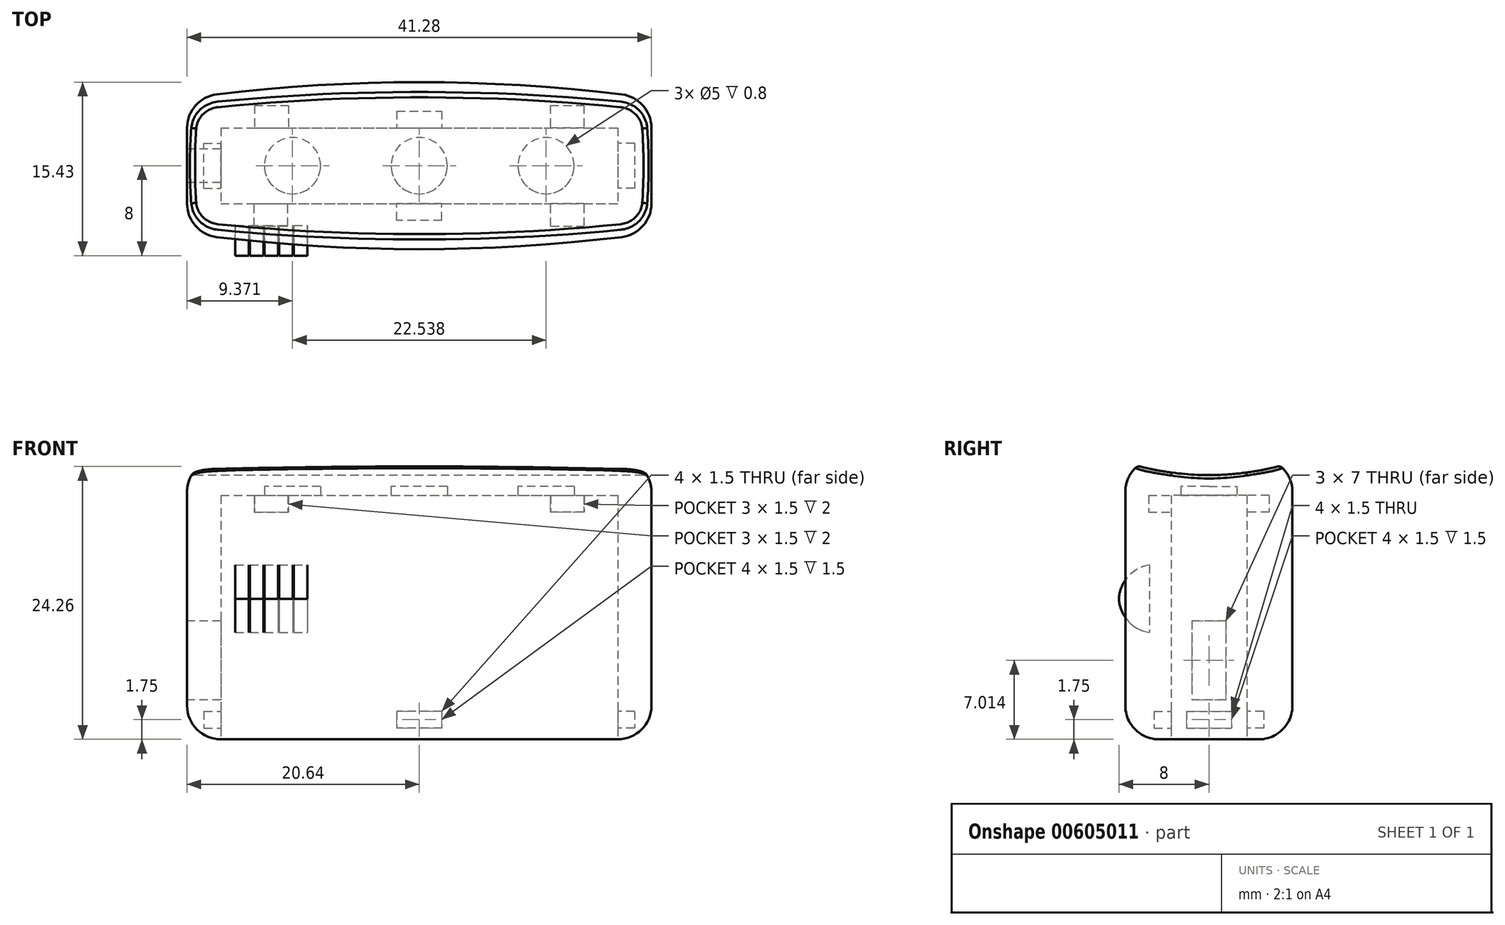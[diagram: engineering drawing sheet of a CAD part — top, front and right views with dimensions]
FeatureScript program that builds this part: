
annotation { "Feature Type Name" : "Feature", "Feature Type Description" : "" }
export const myFeature = defineFeature(function(context is Context, id is Id, definition is map)
    precondition{}
    {
        {
            var Q0;
            Q0=qCreatedBy(makeId("Top.planeOp"),FACE);
            var sketch = newSketch(context, id + "F0", { "sketchPlane" : qUnion([Q0])});
            skLineSegment(sketch, "E0", {"start": v(-20.64, 6) * mm, "end": v(-20.64, -6) * mm});
            skLineSegment(sketch, "E1", {"start": v(20.64, 6) * mm, "end": v(20.64, -6) * mm});
            skArc(sketch, "E2", {"start": v(20.64, 6) * mm, "mid": v(0, 7.43) * mm, "end": v(-20.64, 6) * mm});
            skArc(sketch, "E3.MirrorCS", {"start": v(20.64, -6) * mm, "mid": v(0, -7.43) * mm, "end": v(-20.64, -6) * mm});
            skSolve(sketch);
        }
        {
            var Q0;
            Q0=qSketchRegion(id+"F0",true);
            extrude(context, id + "F1", {"entities" : qUnion([Q0]), "depth" : 25 * mm, "offsetDistance" : 25 * mm});
        }
        {
            var Q0;
            Q0=makeQuery(id+"F1.opExtrude","SWEPT_EDGE",EDGE,{"disambiguationData":[OSD([sQuery(id+"F0.wireOp",EDGE,"E0"),sQuery(id+"F0.wireOp",EDGE,"E2")])]});
            var Q1;
            Q1=makeQuery(id+"F1.opExtrude","SWEPT_EDGE",EDGE,{"disambiguationData":[OSD([sQuery(id+"F0.wireOp",EDGE,"E0"),sQuery(id+"F0.wireOp",EDGE,"E3.MirrorCS")])]});
            var Q2;
            Q2=makeQuery(id+"F1.opExtrude","SWEPT_EDGE",EDGE,{"disambiguationData":[OSD([sQuery(id+"F0.wireOp",EDGE,"E1"),sQuery(id+"F0.wireOp",EDGE,"E2")])]});
            var Q3;
            Q3=makeQuery(id+"F1.opExtrude","SWEPT_EDGE",EDGE,{"disambiguationData":[OSD([sQuery(id+"F0.wireOp",EDGE,"E1"),sQuery(id+"F0.wireOp",EDGE,"E3.MirrorCS")])]});
            var Q4;
            Q4=makeQuery(id+"F1.opExtrude","CAP_EDGE",EDGE,{"disambiguationData":[OSD([sQuery(id+"F0.wireOp",EDGE,"E2")])],"isStart":true});
            var Q5;
            Q5=makeQuery(id+"F1.opExtrude","CAP_EDGE",EDGE,{"disambiguationData":[OSD([sQuery(id+"F0.wireOp",EDGE,"E3.MirrorCS")])],"isStart":true});
            var Q6;
            Q6=makeQuery(id+"F1.opExtrude","CAP_EDGE",EDGE,{"disambiguationData":[OSD([sQuery(id+"F0.wireOp",EDGE,"E0")])],"isStart":true});
            var Q7;
            Q7=makeQuery(id+"F1.opExtrude","CAP_EDGE",EDGE,{"disambiguationData":[OSD([sQuery(id+"F0.wireOp",EDGE,"E1")])],"isStart":true});
            var Q8;
            Q8=makeQuery(id+"F1.opExtrude","CAP_FACE",FACE,{"disambiguationData":[OSD([sQuery(id+"F0.wireOp",EDGE,"E0"),sQuery(id+"F0.wireOp",EDGE,"E1"),sQuery(id+"F0.wireOp",EDGE,"E2"),sQuery(id+"F0.wireOp",EDGE,"E3.MirrorCS")])],"isStart":false});
            fillet(context, id + "F2", {"entities" : qUnion([Q0, Q1, Q2, Q3, Q4, Q5, Q6, Q7, Q8]), "radius" : 3 * mm, "tangentPropagation" : true, "allowEdgeOverflow" : false});
        }
        {
            var Q0;
            Q0=makeQuery(id+"F1.opExtrude","SWEPT_FACE",FACE,{"disambiguationData":[OSD([sQuery(id+"F0.wireOp",EDGE,"E1")])]});
            var sketch = newSketch(context, id + "F3", { "sketchPlane" : qUnion([Q0])});
            skCircle(sketch, "E4", {"center": v(0, 48.5) * mm, "radius": 25 * mm});
            skSolve(sketch);
        }
        {
            var Q0;
            Q0=qSketchRegion(id+"F3",true);
            extrude(context, id + "F4", {"entities" : qUnion([Q0]), "operationType" : NewBodyOperationType.REMOVE, "oppositeDirection" : true, "depth" : 48.9 * mm, "offsetDistance" : 25 * mm});
        }
        {
            var Q0;
            Q0=makeQuery(id+"F1.opExtrude","CAP_FACE",FACE,{"disambiguationData":[OSD([sQuery(id+"F0.wireOp",EDGE,"E0"),sQuery(id+"F0.wireOp",EDGE,"E1"),sQuery(id+"F0.wireOp",EDGE,"E2"),sQuery(id+"F0.wireOp",EDGE,"E3.MirrorCS")])],"isStart":true});
            var sketch = newSketch(context, id + "F5", { "sketchPlane" : qUnion([Q0])});
            skLineSegment(sketch, "E5.bottom", {"start": v(-17.64, 3.36) * mm, "end": v(17.64, 3.36) * mm});
            skLineSegment(sketch, "E5.top", {"start": v(-17.64, -3.36) * mm, "end": v(17.64, -3.36) * mm});
            skLineSegment(sketch, "E5.left", {"start": v(-17.64, 3.36) * mm, "end": v(-17.64, -3.36) * mm});
            skLineSegment(sketch, "E5.right", {"start": v(17.64, 3.36) * mm, "end": v(17.64, -3.36) * mm});
            skSolve(sketch);
        }
        {
            var Q0;
            Q0=qSketchRegion(id+"F5",true);
            extrude(context, id + "F6", {"entities" : qUnion([Q0]), "operationType" : NewBodyOperationType.REMOVE, "oppositeDirection" : true, "depth" : 21.7 * mm, "offsetDistance" : 25 * mm});
        }
        {
            var Q0;
            Q0=makeQuery(id+"F1.opExtrude","SWEPT_FACE",FACE,{"disambiguationData":[OSD([sQuery(id+"F0.wireOp",EDGE,"E0")])]});
            var sketch = newSketch(context, id + "F7", { "sketchPlane" : qUnion([Q0])});
            skLineSegment(sketch, "E6.bottom", {"start": v(-1.5, 10.51) * mm, "end": v(1.5, 10.51) * mm});
            skLineSegment(sketch, "E6.top", {"start": v(-1.5, 3.51) * mm, "end": v(1.5, 3.51) * mm});
            skLineSegment(sketch, "E6.left", {"start": v(-1.5, 10.51) * mm, "end": v(-1.5, 3.51) * mm});
            skLineSegment(sketch, "E6.right", {"start": v(1.5, 10.51) * mm, "end": v(1.5, 3.51) * mm});
            skSolve(sketch);
        }
        {
            var Q0;
            Q0=qSketchRegion(id+"F7",true);
            extrude(context, id + "F8", {"entities" : qUnion([Q0]), "operationType" : NewBodyOperationType.REMOVE, "oppositeDirection" : true, "depth" : 25 * mm, "offsetDistance" : 25 * mm});
        }
        {
            var Q0;
            Q0=makeQuery(id+"F4.boolean.opBoolean","COPY",FACE,{"derivedFrom":makeQuery(id+"F4.opExtrude","SWEPT_FACE",FACE,{"disambiguationData":[OSD([sQuery(id+"F3.wireOp",EDGE,"E4")])]})});
            fillet(context, id + "F9", {"entities" : qUnion([Q0]), "radius" : 0.5 * mm, "tangentPropagation" : true, "allowEdgeOverflow" : false});
        }
        {
            var Q0;
            Q0=qCreatedBy(makeId("Front.planeOp"),FACE);
            var sketch = newSketch(context, id + "F10", { "sketchPlane" : qUnion([Q0])});
            skLineSegment(sketch, "E7.bottom", {"start": v(-15.04, 15.5) * mm, "end": v(-13.84, 15.5) * mm});
            skLineSegment(sketch, "E7.top", {"start": v(-15.04, 9.5) * mm, "end": v(-13.84, 9.5) * mm});
            skLineSegment(sketch, "E7.left", {"start": v(-15.04, 15.5) * mm, "end": v(-15.04, 9.5) * mm});
            skLineSegment(sketch, "E7.right", {"start": v(-13.84, 15.5) * mm, "end": v(-13.84, 9.5) * mm});
            skLineSegment(sketch, "E8.bottom", {"start": v(-13.74, 15.5) * mm, "end": v(-12.54, 15.5) * mm});
            skLineSegment(sketch, "E8.top", {"start": v(-13.74, 9.5) * mm, "end": v(-12.54, 9.5) * mm});
            skLineSegment(sketch, "E8.left", {"start": v(-13.74, 15.5) * mm, "end": v(-13.74, 9.5) * mm});
            skLineSegment(sketch, "E8.right", {"start": v(-12.54, 15.5) * mm, "end": v(-12.54, 9.5) * mm});
            skLineSegment(sketch, "E9.bottom", {"start": v(-12.44, 15.5) * mm, "end": v(-11.24, 15.5) * mm});
            skLineSegment(sketch, "E9.top", {"start": v(-12.44, 9.5) * mm, "end": v(-11.24, 9.5) * mm});
            skLineSegment(sketch, "E9.left", {"start": v(-12.44, 15.5) * mm, "end": v(-12.44, 9.5) * mm});
            skLineSegment(sketch, "E9.right", {"start": v(-11.24, 15.5) * mm, "end": v(-11.24, 9.5) * mm});
            skLineSegment(sketch, "E10.bottom", {"start": v(-11.14, 15.5) * mm, "end": v(-9.94, 15.5) * mm});
            skLineSegment(sketch, "E10.top", {"start": v(-11.14, 9.5) * mm, "end": v(-9.94, 9.5) * mm});
            skLineSegment(sketch, "E10.left", {"start": v(-11.14, 15.5) * mm, "end": v(-11.14, 9.5) * mm});
            skLineSegment(sketch, "E10.right", {"start": v(-9.94, 15.5) * mm, "end": v(-9.94, 9.5) * mm});
            skLineSegment(sketch, "E11.bottom", {"start": v(-16.34, 15.5) * mm, "end": v(-15.14, 15.5) * mm});
            skLineSegment(sketch, "E11.top", {"start": v(-16.34, 9.5) * mm, "end": v(-15.14, 9.5) * mm});
            skLineSegment(sketch, "E11.left", {"start": v(-16.34, 15.5) * mm, "end": v(-16.34, 9.5) * mm});
            skLineSegment(sketch, "E11.right", {"start": v(-15.14, 15.5) * mm, "end": v(-15.14, 9.5) * mm});
            skLineSegment(sketch, "E12.left", {"start": v(-9.94, 13) * mm, "end": v(-9.94, 11.9) * mm});
            skSolve(sketch);
        }
        {
            var Q0;
            Q0=qSketchRegion(id+"F10",true);
            extrude(context, id + "F11", {"entities" : qUnion([Q0]), "depth" : 8 * mm, "offsetDistance" : 25 * mm, "hasSecondDirection" : true, "secondDirectionOppositeDirection" : false, "secondDirectionDepth" : 5.3 * mm});
        }
        {
            var Q0;
            Q0=makeQuery(id+"F11.opExtrude","CAP_EDGE",EDGE,{"disambiguationData":[OSD([sQuery(id+"F10.wireOp",EDGE,"E11.bottom")])],"isStart":false});
            var Q1;
            Q1=makeQuery(id+"F11.opExtrude","CAP_EDGE",EDGE,{"disambiguationData":[OSD([sQuery(id+"F10.wireOp",EDGE,"E7.bottom")])],"isStart":false});
            var Q2;
            Q2=makeQuery(id+"F11.opExtrude","CAP_EDGE",EDGE,{"disambiguationData":[OSD([sQuery(id+"F10.wireOp",EDGE,"E8.bottom")])],"isStart":false});
            var Q3;
            Q3=makeQuery(id+"F11.opExtrude","CAP_EDGE",EDGE,{"disambiguationData":[OSD([sQuery(id+"F10.wireOp",EDGE,"E9.bottom")])],"isStart":false});
            var Q4;
            Q4=makeQuery(id+"F11.opExtrude","CAP_EDGE",EDGE,{"disambiguationData":[OSD([sQuery(id+"F10.wireOp",EDGE,"E10.bottom")])],"isStart":false});
            var Q5;
            Q5=makeQuery(id+"F11.opExtrude","CAP_EDGE",EDGE,{"disambiguationData":[OSD([sQuery(id+"F10.wireOp",EDGE,"E10.top")])],"isStart":false});
            var Q6;
            Q6=makeQuery(id+"F11.opExtrude","CAP_EDGE",EDGE,{"disambiguationData":[OSD([sQuery(id+"F10.wireOp",EDGE,"E9.top")])],"isStart":false});
            var Q7;
            Q7=makeQuery(id+"F11.opExtrude","CAP_EDGE",EDGE,{"disambiguationData":[OSD([sQuery(id+"F10.wireOp",EDGE,"E8.top")])],"isStart":false});
            var Q8;
            Q8=makeQuery(id+"F11.opExtrude","CAP_EDGE",EDGE,{"disambiguationData":[OSD([sQuery(id+"F10.wireOp",EDGE,"E7.top")])],"isStart":false});
            var Q9;
            Q9=makeQuery(id+"F11.opExtrude","CAP_EDGE",EDGE,{"disambiguationData":[OSD([sQuery(id+"F10.wireOp",EDGE,"E11.top")])],"isStart":false});
            fillet(context, id + "F12", {"entities" : qUnion([Q0, Q1, Q2, Q3, Q4, Q5, Q6, Q7, Q8, Q9]), "radius" : 3.2 * mm, "tangentPropagation" : true, "allowEdgeOverflow" : false});
        }
        {
            var Q0;
            Q0=qCreatedBy(makeId("Top.planeOp"),FACE);
            var sketch = newSketch(context, id + "F13", { "sketchPlane" : qUnion([Q0])});
            skCircle(sketch, "E13", {"center": v(-11.27, 0) * mm, "radius": 2.5 * mm});
            skCircle(sketch, "E14", {"center": v(0, 0) * mm, "radius": 2.5 * mm});
            skCircle(sketch, "E15.MirrorC", {"center": v(11.27, 0) * mm, "radius": 2.5 * mm});
            skSolve(sketch);
        }
        {
            var Q0;
            Q0=qSketchRegion(id+"F13",true);
            extrude(context, id + "F14", {"entities" : qUnion([Q0]), "operationType" : NewBodyOperationType.REMOVE, "depth" : 22.5 * mm, "offsetDistance" : 25 * mm});
        }
        {
            var Q0;
            Q0=makeQuery(id+"F6.boolean.opBoolean","COPY",FACE,{"derivedFrom":makeQuery(id+"F6.opExtrude","SWEPT_FACE",FACE,{"disambiguationData":[OSD([sQuery(id+"F5.wireOp",EDGE,"E5.top")])]})});
            var sketch = newSketch(context, id + "F15", { "sketchPlane" : qUnion([Q0])});
            skLineSegment(sketch, "E16.bottom", {"start": v(-14.64, 21.7) * mm, "end": v(-11.64, 21.7) * mm});
            skLineSegment(sketch, "E16.top", {"start": v(-14.64, 20.2) * mm, "end": v(-11.64, 20.2) * mm});
            skLineSegment(sketch, "E16.left", {"start": v(-14.64, 21.7) * mm, "end": v(-14.64, 20.2) * mm});
            skLineSegment(sketch, "E16.right", {"start": v(-11.64, 21.7) * mm, "end": v(-11.64, 20.2) * mm});
            skLineSegment(sketch, "E17.MirrorCS", {"start": v(14.64, 20.2) * mm, "end": v(11.64, 20.2) * mm});
            skLineSegment(sketch, "E18.MirrorCS", {"start": v(11.64, 21.7) * mm, "end": v(11.64, 20.2) * mm});
            skLineSegment(sketch, "E19.MirrorCS", {"start": v(14.64, 21.7) * mm, "end": v(14.64, 20.2) * mm});
            skLineSegment(sketch, "E20", {"start": v(11.64, 21.7) * mm, "end": v(14.64, 21.7) * mm});
            skSolve(sketch);
        }
        {
            var Q0;
            Q0=qSketchRegion(id+"F15",true);
            extrude(context, id + "F16", {"entities" : qUnion([Q0]), "operationType" : NewBodyOperationType.REMOVE, "oppositeDirection" : true, "depth" : 2 * mm, "offsetDistance" : 25 * mm});
        }
        {
            var Q0;
            Q0=makeQuery(id+"F6.boolean.opBoolean","COPY",FACE,{"derivedFrom":makeQuery(id+"F6.opExtrude","SWEPT_FACE",FACE,{"disambiguationData":[OSD([sQuery(id+"F5.wireOp",EDGE,"E5.bottom")])]})});
            var sketch = newSketch(context, id + "F17", { "sketchPlane" : qUnion([Q0])});
            skLineSegment(sketch, "E21.bottom", {"start": v(-14.68, 21.7) * mm, "end": v(-11.68, 21.7) * mm});
            skLineSegment(sketch, "E21.top", {"start": v(-14.68, 20.2) * mm, "end": v(-11.68, 20.2) * mm});
            skLineSegment(sketch, "E21.left", {"start": v(-14.68, 21.7) * mm, "end": v(-14.68, 20.2) * mm});
            skLineSegment(sketch, "E21.right", {"start": v(-11.68, 21.7) * mm, "end": v(-11.68, 20.2) * mm});
            skLineSegment(sketch, "E22.MirrorCS", {"start": v(14.68, 21.7) * mm, "end": v(11.68, 21.7) * mm});
            skLineSegment(sketch, "E23.MirrorCS", {"start": v(14.68, 20.2) * mm, "end": v(11.68, 20.2) * mm});
            skLineSegment(sketch, "E24.MirrorCS", {"start": v(14.68, 21.7) * mm, "end": v(14.68, 20.2) * mm});
            skLineSegment(sketch, "E25.MirrorCS", {"start": v(11.68, 21.7) * mm, "end": v(11.68, 20.2) * mm});
            skSolve(sketch);
        }
        {
            var Q0;
            Q0=qSketchRegion(id+"F17",true);
            extrude(context, id + "F18", {"entities" : qUnion([Q0]), "operationType" : NewBodyOperationType.REMOVE, "oppositeDirection" : true, "depth" : 2 * mm, "offsetDistance" : 25 * mm});
        }
        {
            var Q0;
            Q0=makeQuery(id+"F6.boolean.opBoolean","COPY",FACE,{"derivedFrom":makeQuery(id+"F6.opExtrude","SWEPT_FACE",FACE,{"disambiguationData":[OSD([sQuery(id+"F5.wireOp",EDGE,"E5.right")])]})});
            var sketch = newSketch(context, id + "F19", { "sketchPlane" : qUnion([Q0])});
            skLineSegment(sketch, "E26.bottom", {"start": v(-2, 2.5) * mm, "end": v(2, 2.5) * mm});
            skLineSegment(sketch, "E26.top", {"start": v(-2, 1) * mm, "end": v(2, 1) * mm});
            skLineSegment(sketch, "E26.left", {"start": v(-2, 2.5) * mm, "end": v(-2, 1) * mm});
            skLineSegment(sketch, "E26.right", {"start": v(2, 2.5) * mm, "end": v(2, 1) * mm});
            skSolve(sketch);
        }
        {
            var Q0;
            Q0=qSketchRegion(id+"F19",true);
            extrude(context, id + "F20", {"entities" : qUnion([Q0]), "operationType" : NewBodyOperationType.REMOVE, "oppositeDirection" : true, "depth" : 1.5 * mm, "offsetDistance" : 25 * mm});
        }
        {
            var Q0;
            Q0=makeQuery(id+"F6.boolean.opBoolean","COPY",FACE,{"derivedFrom":makeQuery(id+"F6.opExtrude","SWEPT_FACE",FACE,{"disambiguationData":[OSD([sQuery(id+"F5.wireOp",EDGE,"E5.left")])]})});
            var sketch = newSketch(context, id + "F21", { "sketchPlane" : qUnion([Q0])});
            skLineSegment(sketch, "E27.bottom", {"start": v(-2, 2.5) * mm, "end": v(2, 2.5) * mm});
            skLineSegment(sketch, "E27.top", {"start": v(-2, 1) * mm, "end": v(2, 1) * mm});
            skLineSegment(sketch, "E27.left", {"start": v(-2, 2.5) * mm, "end": v(-2, 1) * mm});
            skLineSegment(sketch, "E27.right", {"start": v(2, 2.5) * mm, "end": v(2, 1) * mm});
            skSolve(sketch);
        }
        {
            var Q0;
            Q0=qSketchRegion(id+"F21",true);
            extrude(context, id + "F22", {"entities" : qUnion([Q0]), "operationType" : NewBodyOperationType.REMOVE, "oppositeDirection" : true, "depth" : 1.5 * mm, "offsetDistance" : 25 * mm});
        }
        {
            var Q0;
            Q0=makeQuery(id+"F6.boolean.opBoolean","COPY",FACE,{"derivedFrom":makeQuery(id+"F6.opExtrude","SWEPT_FACE",FACE,{"disambiguationData":[OSD([sQuery(id+"F5.wireOp",EDGE,"E5.top")])]})});
            var sketch = newSketch(context, id + "F23", { "sketchPlane" : qUnion([Q0])});
            skLineSegment(sketch, "E28.bottom", {"start": v(-2, 2.5) * mm, "end": v(2, 2.5) * mm});
            skLineSegment(sketch, "E28.top", {"start": v(-2, 1) * mm, "end": v(2, 1) * mm});
            skLineSegment(sketch, "E28.left", {"start": v(-2, 2.5) * mm, "end": v(-2, 1) * mm});
            skLineSegment(sketch, "E28.right", {"start": v(2, 2.5) * mm, "end": v(2, 1) * mm});
            skSolve(sketch);
        }
        {
            var Q0;
            Q0=qSketchRegion(id+"F23",true);
            extrude(context, id + "F24", {"entities" : qUnion([Q0]), "operationType" : NewBodyOperationType.REMOVE, "oppositeDirection" : true, "depth" : 1.5 * mm, "offsetDistance" : 25 * mm});
        }
        {
            var Q0;
            Q0=makeQuery(id+"F6.boolean.opBoolean","COPY",FACE,{"derivedFrom":makeQuery(id+"F6.opExtrude","SWEPT_FACE",FACE,{"disambiguationData":[OSD([sQuery(id+"F5.wireOp",EDGE,"E5.bottom")])]})});
            var sketch = newSketch(context, id + "F25", { "sketchPlane" : qUnion([Q0])});
            skLineSegment(sketch, "E29.bottom", {"start": v(-2, 2.5) * mm, "end": v(2, 2.5) * mm});
            skLineSegment(sketch, "E29.top", {"start": v(-2, 1) * mm, "end": v(2, 1) * mm});
            skLineSegment(sketch, "E29.left", {"start": v(-2, 2.5) * mm, "end": v(-2, 1) * mm});
            skLineSegment(sketch, "E29.right", {"start": v(2, 2.5) * mm, "end": v(2, 1) * mm});
            skSolve(sketch);
        }
        {
            var Q0;
            Q0=qSketchRegion(id+"F25",true);
            extrude(context, id + "F26", {"entities" : qUnion([Q0]), "operationType" : NewBodyOperationType.REMOVE, "oppositeDirection" : true, "depth" : 1.5 * mm, "offsetDistance" : 25 * mm});
        }
    });
